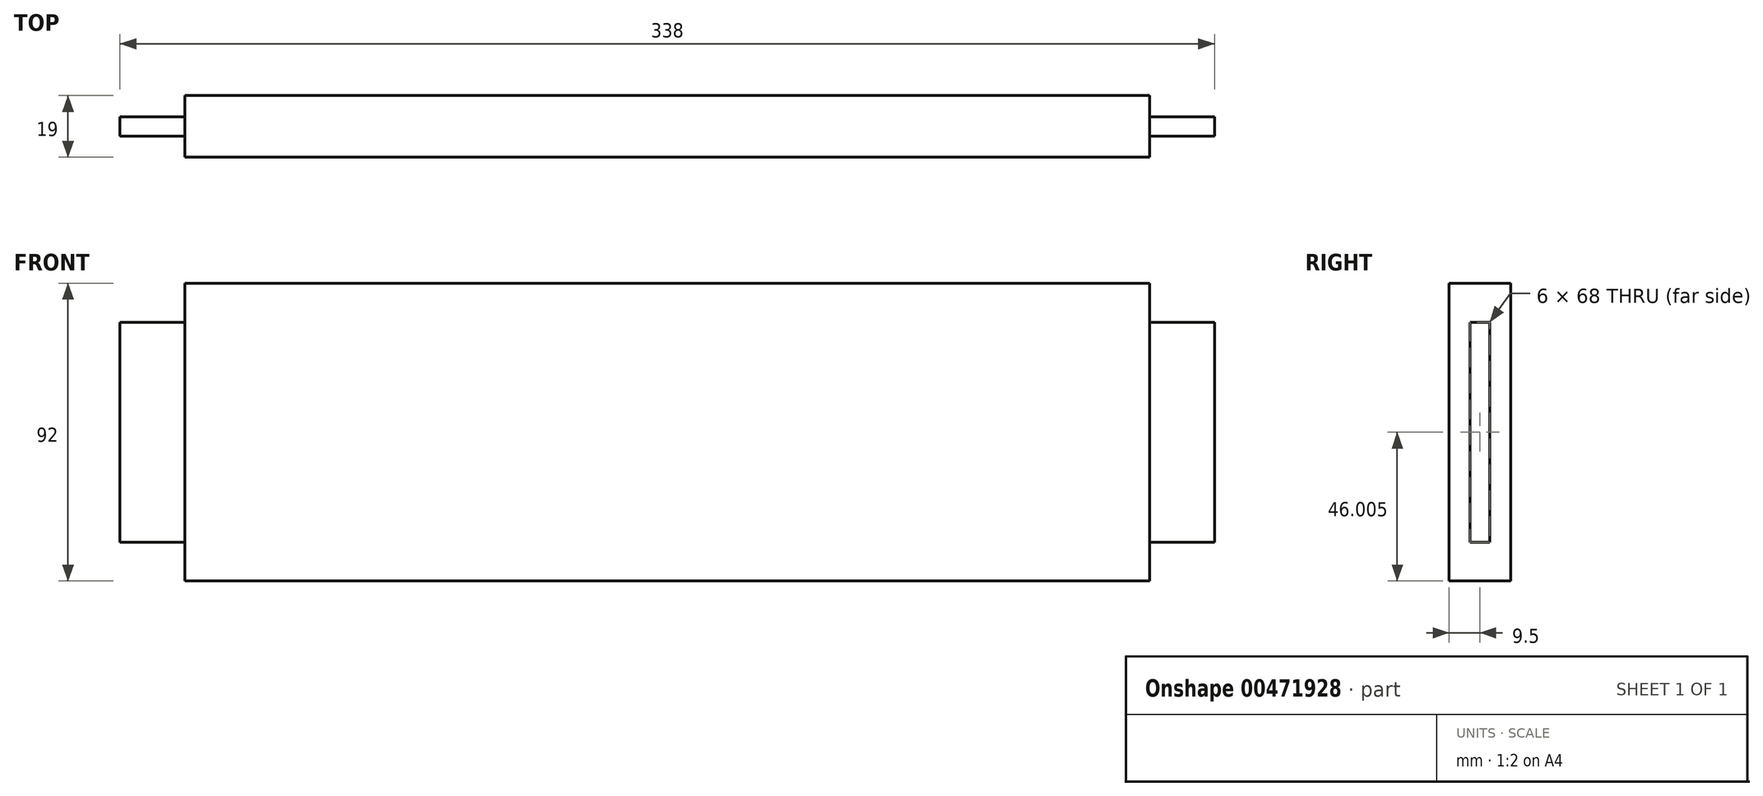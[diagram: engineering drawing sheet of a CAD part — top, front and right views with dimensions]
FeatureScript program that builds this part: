
annotation { "Feature Type Name" : "Feature", "Feature Type Description" : "" }
export const myFeature = defineFeature(function(context is Context, id is Id, definition is map)
    precondition{}
    {
        {
            var Q0;
            Q0=qCreatedBy(makeId("Front.planeOp"),FACE);
            var sketch = newSketch(context, id + "F0", { "sketchPlane" : qUnion([Q0])});
            skLineSegment(sketch, "E0", {"start": v(-85.72, 69.1) * mm, "end": v(-85.72, 1.1) * mm});
            skLineSegment(sketch, "E1", {"start": v(-65.72, -10.9) * mm, "end": v(232.28, -10.9) * mm});
            skLineSegment(sketch, "E2", {"start": v(252.28, 1.1) * mm, "end": v(252.28, 69.1) * mm});
            skLineSegment(sketch, "E3", {"start": v(232.28, 81.1) * mm, "end": v(-65.72, 81.1) * mm});
            skLineSegment(sketch, "E4", {"start": v(-65.72, 81.1) * mm, "end": v(-65.72, 69.1) * mm});
            skLineSegment(sketch, "E5", {"start": v(-65.72, 69.1) * mm, "end": v(-85.72, 69.1) * mm});
            skLineSegment(sketch, "E6", {"start": v(-65.72, -10.9) * mm, "end": v(-65.72, 1.1) * mm});
            skLineSegment(sketch, "E7", {"start": v(-65.72, 1.1) * mm, "end": v(-85.72, 1.1) * mm});
            skPoint(sketch, "E8.orphan", {"position": v(-85.72, 81.1) * mm});
            skPoint(sketch, "E9.orphan", {"position": v(-85.72, -10.9) * mm});
            skLineSegment(sketch, "E10", {"start": v(232.28, 81.1) * mm, "end": v(232.28, 69.1) * mm});
            skLineSegment(sketch, "E11", {"start": v(232.28, 69.1) * mm, "end": v(252.28, 69.1) * mm});
            skPoint(sketch, "E12.orphan", {"position": v(252.28, 81.1) * mm});
            skLineSegment(sketch, "E13", {"start": v(232.28, -10.9) * mm, "end": v(232.28, 1.1) * mm});
            skLineSegment(sketch, "E14", {"start": v(232.28, 1.1) * mm, "end": v(252.28, 1.1) * mm});
            skPoint(sketch, "E15.orphan", {"position": v(252.28, -10.9) * mm});
            skSolve(sketch);
        }
        {
            var Q0;
            Q0 = qSketchRegion(id + "F0", true);
            extrude(context, id + "F1", {"entities" : qUnion([Q0]), "depth" : 19 * mm});
        }
        {
            var Q0;
            Q0=makeQuery(id+"F1.opExtrude","SWEPT_FACE",FACE,{"disambiguationData":[OSD([sQuery(id+"F0.wireOp",EDGE,"E2")])]});
            var sketch = newSketch(context, id + "F2", { "sketchPlane" : qUnion([Q0])});
            skLineSegment(sketch, "E16", {"start": v(-19, 69.1) * mm, "end": v(-12.5, 69.1) * mm});
            skLineSegment(sketch, "E17", {"start": v(-6.5, 69.1) * mm, "end": v(0, 69.1) * mm});
            skLineSegment(sketch, "E18", {"start": v(-19, 69.1) * mm, "end": v(-19, 1.1) * mm});
            skLineSegment(sketch, "E19", {"start": v(-19, 1.1) * mm, "end": v(-12.5, 1.1) * mm});
            skLineSegment(sketch, "E20", {"start": v(-12.5, 1.1) * mm, "end": v(-12.5, 69.1) * mm});
            skLineSegment(sketch, "E21", {"start": v(-6.5, 1.1) * mm, "end": v(-6.5, 69.1) * mm});
            skLineSegment(sketch, "E22", {"start": v(-6.5, 1.1) * mm, "end": v(0, 1.1) * mm});
            skLineSegment(sketch, "E23", {"start": v(0, 1.1) * mm, "end": v(0, 69.1) * mm});
            skSolve(sketch);
        }
        {
            var Q0;
            Q0 = qSketchRegion(id + "F2", true);
            extrude(context, id + "F3", {"entities" : qUnion([Q0]), "operationType" : NewBodyOperationType.REMOVE, "oppositeDirection" : true, "depth" : 20 * mm});
        }
        {
            var Q0;
            Q0=makeQuery(id+"F1.opExtrude","SWEPT_FACE",FACE,{"disambiguationData":[OSD([sQuery(id+"F0.wireOp",EDGE,"E0")])]});
            var sketch = newSketch(context, id + "F4", { "sketchPlane" : qUnion([Q0])});
            skLineSegment(sketch, "E24", {"start": v(0, 69.1) * mm, "end": v(6.5, 69.1) * mm});
            skLineSegment(sketch, "E25", {"start": v(6.5, 69.1) * mm, "end": v(6.5, 1.1) * mm});
            skLineSegment(sketch, "E26", {"start": v(12.5, 1.1) * mm, "end": v(12.5, 69.1) * mm});
            skLineSegment(sketch, "E27", {"start": v(12.5, 69.1) * mm, "end": v(19, 69.1) * mm});
            skLineSegment(sketch, "E28", {"start": v(19, 69.1) * mm, "end": v(19, 1.1) * mm});
            skLineSegment(sketch, "E29", {"start": v(19, 1.1) * mm, "end": v(12.5, 1.1) * mm});
            skLineSegment(sketch, "E30", {"start": v(0, 69.1) * mm, "end": v(0, 1.1) * mm});
            skLineSegment(sketch, "E31", {"start": v(0, 1.1) * mm, "end": v(6.5, 1.1) * mm});
            skSolve(sketch);
        }
        {
            var Q0;
            Q0 = qSketchRegion(id + "F4", true);
            extrude(context, id + "F5", {"entities" : qUnion([Q0]), "operationType" : NewBodyOperationType.REMOVE, "oppositeDirection" : true, "depth" : 20 * mm});
        }
    });
